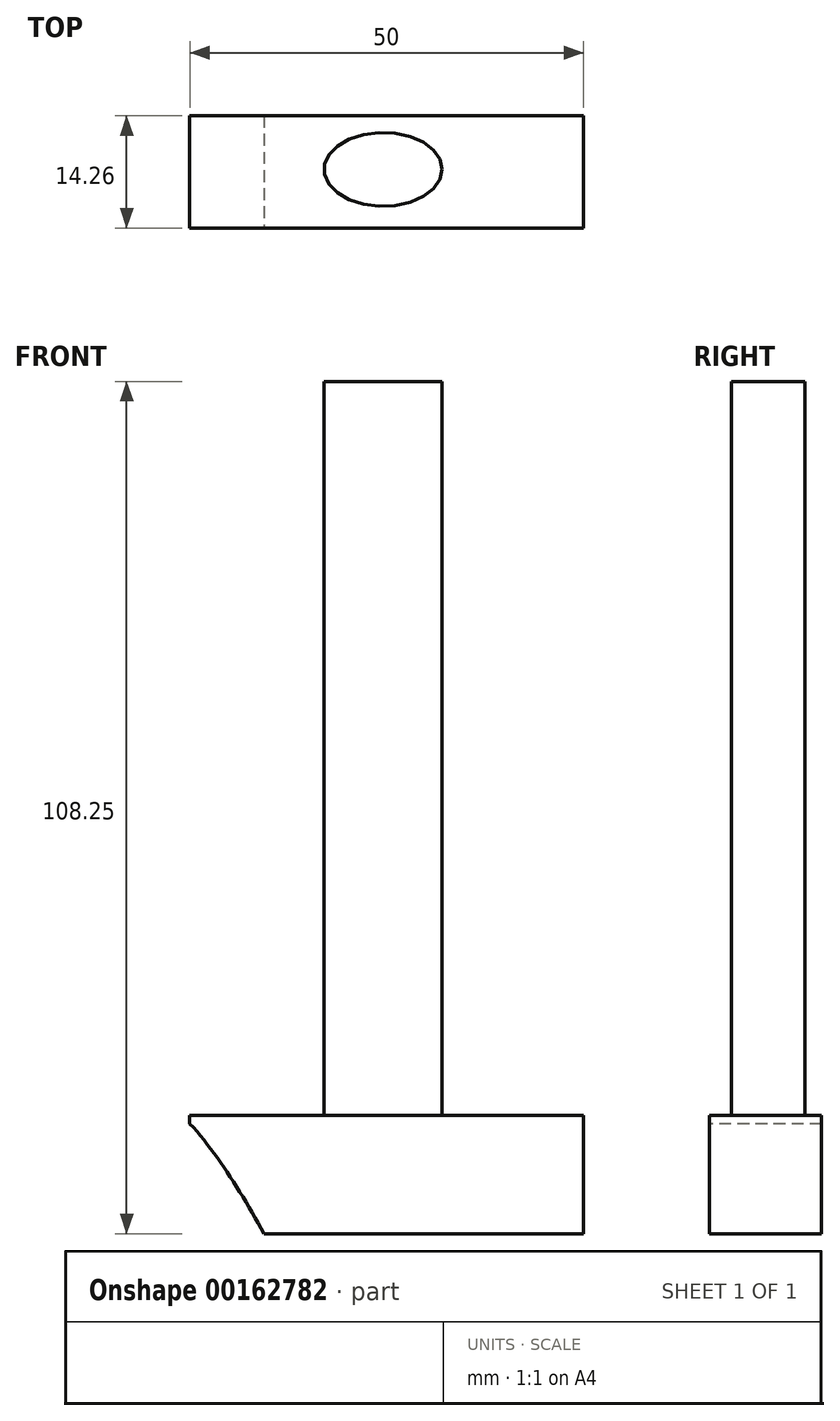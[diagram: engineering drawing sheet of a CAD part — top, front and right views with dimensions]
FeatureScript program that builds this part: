
annotation { "Feature Type Name" : "Feature", "Feature Type Description" : "" }
export const myFeature = defineFeature(function(context is Context, id is Id, definition is map)
    precondition{}
    {
        {
            var Q0;
            Q0=qCreatedBy(makeId("Top.planeOp"),FACE);
            var sketch = newSketch(context, id + "F0", { "sketchPlane" : qUnion([Q0])});
            skLineSegment(sketch, "E0.bottom", {"start": v(-24.56, 6.8) * mm, "end": v(25.44, 6.8) * mm});
            skLineSegment(sketch, "E0.top", {"start": v(-24.56, -7.46) * mm, "end": v(25.44, -7.46) * mm});
            skLineSegment(sketch, "E0.left", {"start": v(-24.56, 6.8) * mm, "end": v(-24.56, -7.46) * mm});
            skLineSegment(sketch, "E0.right", {"start": v(25.44, 6.8) * mm, "end": v(25.44, -7.46) * mm});
            skEllipse(sketch, "E1", {"center": v(0, 0) * mm, "majorRadius": 7.5 * mm, "minorRadius": 4.69 * mm, "majorAxis": v(1, 0)});
            skSolve(sketch);
        }
        {
            var Q0;
            Q0=makeQuery(id+"F0.imprint","IMPRINT",FACE,{"disambiguationData":[TD([[makeQuery(id+"F0.imprint","IMPRINT",EDGE,{"derivedFrom":sQuery(id+"F0.wireOp",EDGE,"E1")}),1.0]])]});
            extrude(context, id + "F1", {"entities" : qUnion([Q0]), "depth" : 108.25 * mm});
        }
        {
            var Q0;
            Q0=makeQuery(id+"F0.imprint","IMPRINT",FACE,{"disambiguationData":[TD([[makeQuery(id+"F0.imprint","IMPRINT",EDGE,{"derivedFrom":sQuery(id+"F0.wireOp",EDGE,"E0.bottom")}),-1.0]])]});
            extrude(context, id + "F2", {"entities" : qUnion([Q0]), "operationType" : NewBodyOperationType.ADD, "depth" : 15 * mm});
        }
        {
            var Q0;
            Q0=qCreatedBy(makeId("Front.planeOp"),FACE);
            var sketch = newSketch(context, id + "F3", { "sketchPlane" : qUnion([Q0])});
            skFitSpline(sketch, "E2", {"points": [v(-13.72, -2.45) * mm, v(-43.07, 19.34) * mm, v(-103.56, -35.21) * mm, v(-103.38, -34.5) * mm], "startDerivative": vector(-58.82, 104.74) * mm, "endDerivative": vector(9.33, 21.17) * mm});
            skLineSegment(sketch, "E3", {"start": v(-13.72, -2.45) * mm, "end": v(-103.55, -34.88) * mm});
            skSolve(sketch);
        }
        {
            var Q0;
            {var subQ0=sQuery(id+"F3.wireOp",EDGE,"E3");var subQ1=sQuery(id+"F3.wireOp",EDGE,"E2");var subQ2=makeQuery(id+"F3.imprint","INTERSECT",VERTEX,{"disambiguationData":[OD(0.0)],"derivedFrom":[subQ1,subQ0]});Q0=makeQuery(id+"F3.imprint","IMPRINT",FACE,{"disambiguationData":[TD([[makeQuery(id+"F3.imprint","IMPRINT",EDGE,{"disambiguationData":[TD([[subQ2,-1.0]])],"derivedFrom":subQ1}),1.0]])]});}
            extrude(context, id + "F4", {"entities" : qUnion([Q0]), "operationType" : NewBodyOperationType.REMOVE, "oppositeDirection" : true, "depth" : 25 * mm, "hasSecondDirection" : true, "secondDirectionOppositeDirection" : false, "secondDirectionDepth" : 25 * mm});
        }
    });
